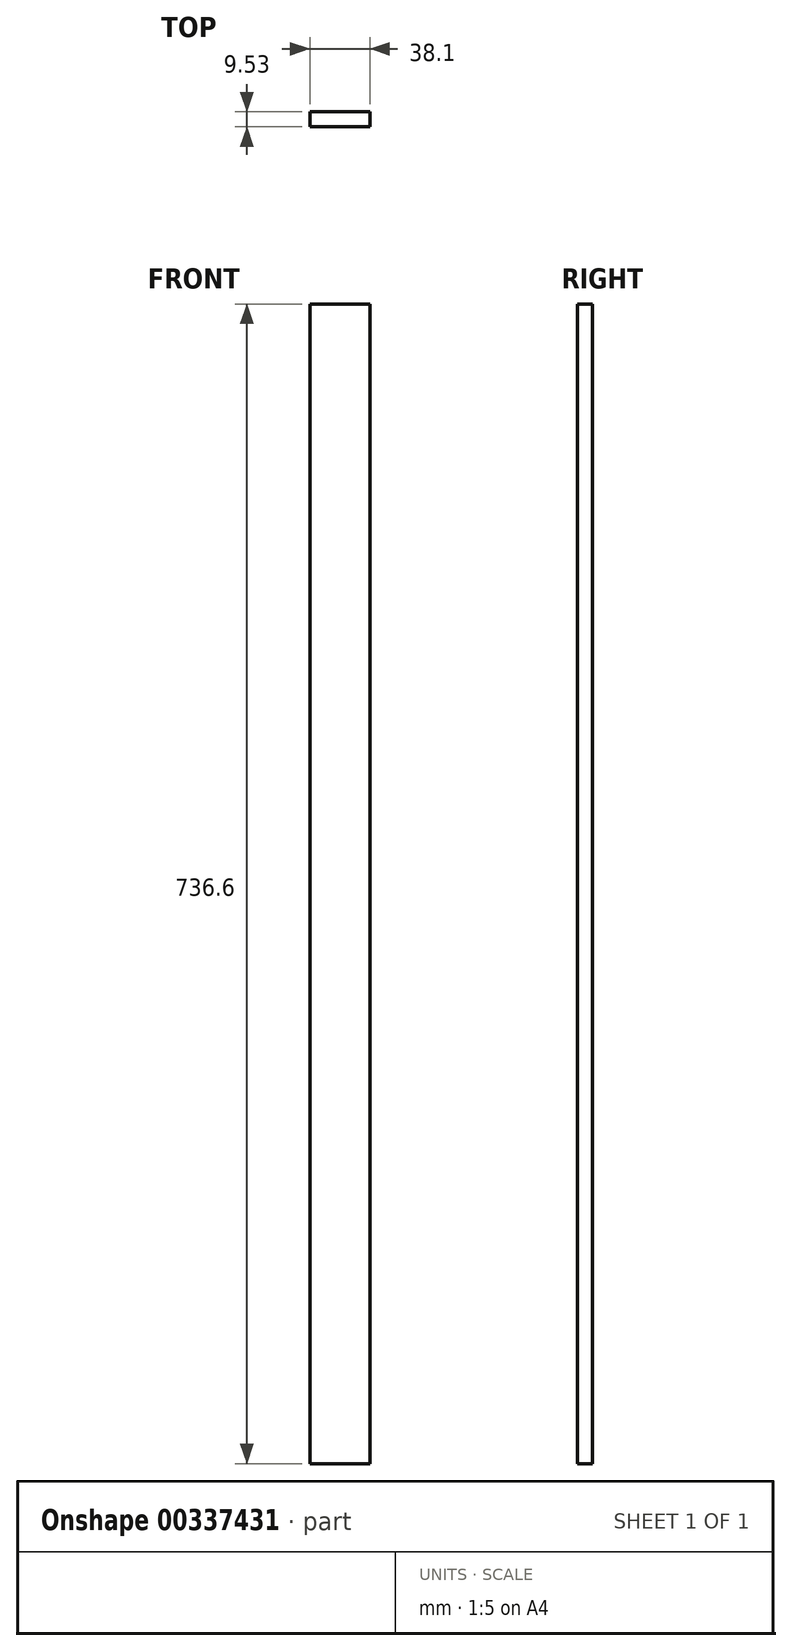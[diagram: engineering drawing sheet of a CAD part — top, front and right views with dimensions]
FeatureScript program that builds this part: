
annotation { "Feature Type Name" : "Feature", "Feature Type Description" : "" }
export const myFeature = defineFeature(function(context is Context, id is Id, definition is map)
    precondition{}
    {
        {
            var Q0;
            Q0=qCreatedBy(makeId("Front.planeOp"),FACE);
            var sketch = newSketch(context, id + "F0", { "sketchPlane" : qUnion([Q0])});
            skLineSegment(sketch, "E0.bottom", {"start": v(0, 0) * mm, "end": v(38.1, 0) * mm});
            skLineSegment(sketch, "E0.top", {"start": v(0, -736.6) * mm, "end": v(38.1, -736.6) * mm});
            skLineSegment(sketch, "E0.left", {"start": v(0, 0) * mm, "end": v(0, -736.6) * mm});
            skLineSegment(sketch, "E0.right", {"start": v(38.1, 0) * mm, "end": v(38.1, -736.6) * mm});
            skSolve(sketch);
        }
        {
            var Q0;
            Q0 = qSketchRegion(id + "F0", true);
            extrude(context, id + "F1", {"entities" : qUnion([Q0]), "depth" : 9.52 * mm});
        }
    });
